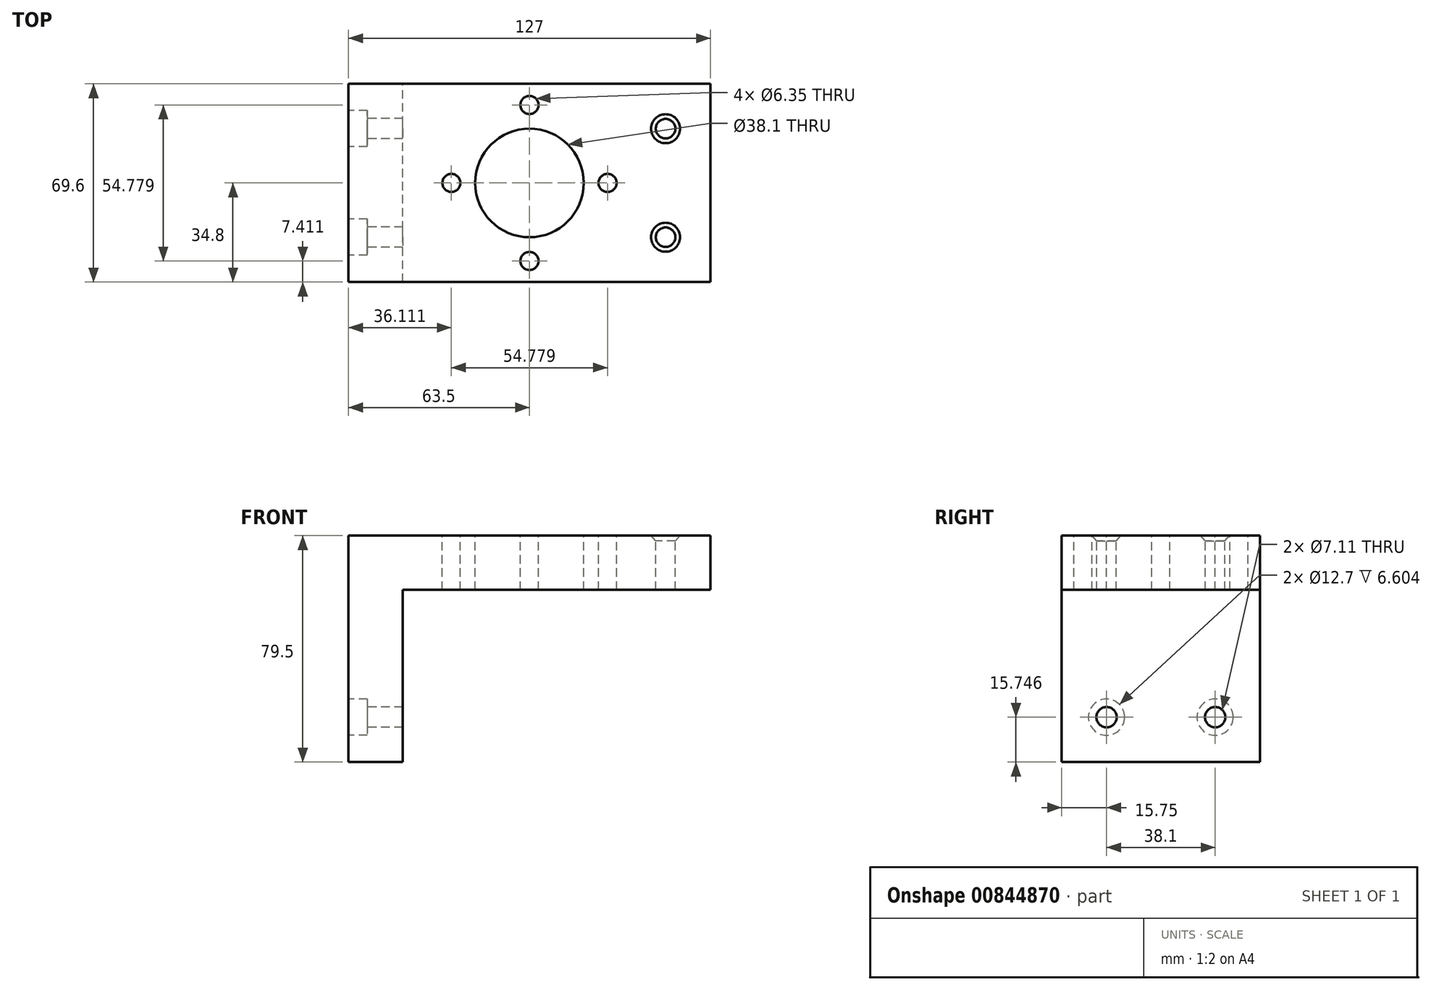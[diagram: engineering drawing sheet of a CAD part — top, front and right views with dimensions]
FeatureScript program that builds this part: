
annotation { "Feature Type Name" : "Feature", "Feature Type Description" : "" }
export const myFeature = defineFeature(function(context is Context, id is Id, definition is map)
    precondition{}
    {
        {
            var Q0;
            Q0=qCreatedBy(makeId("Top.planeOp"),FACE);
            var sketch = newSketch(context, id + "F0", { "sketchPlane" : qUnion([Q0])});
            skLineSegment(sketch, "E0.bottom", {"start": v(63.5, 34.8) * mm, "end": v(-63.5, 34.8) * mm});
            skLineSegment(sketch, "E0.top", {"start": v(63.5, -34.8) * mm, "end": v(-63.5, -34.8) * mm});
            skLineSegment(sketch, "E0.left", {"start": v(63.5, 34.8) * mm, "end": v(63.5, -34.8) * mm});
            skLineSegment(sketch, "E0.right", {"start": v(-63.5, 34.8) * mm, "end": v(-63.5, -34.8) * mm});
            skPoint(sketch, "E0.middle", {"position": v(0, 0) * mm});
            skSolve(sketch);
        }
        {
            var Q0;
            Q0 = qSketchRegion(id + "F0", true);
            extrude(context, id + "F1", {"entities" : qUnion([Q0]), "oppositeDirection" : true, "depth" : 19.05 * mm, "offsetDistance" : 25.4 * mm});
        }
        {
            var Q0;
            Q0=makeQuery(id+"F1.opExtrude","CAP_FACE",FACE,{"disambiguationData":[OSD([sQuery(id+"F0.wireOp",EDGE,"E0.bottom"),sQuery(id+"F0.wireOp",EDGE,"E0.top"),sQuery(id+"F0.wireOp",EDGE,"E0.left"),sQuery(id+"F0.wireOp",EDGE,"E0.right")])],"isStart":false});
            var sketch = newSketch(context, id + "F2", { "sketchPlane" : qUnion([Q0])});
            skLineSegment(sketch, "E1.bottom", {"start": v(-63.5, 34.8) * mm, "end": v(-44.45, 34.8) * mm});
            skLineSegment(sketch, "E1.top", {"start": v(-63.5, -34.8) * mm, "end": v(-44.45, -34.8) * mm});
            skLineSegment(sketch, "E1.left", {"start": v(-63.5, 34.8) * mm, "end": v(-63.5, -34.8) * mm});
            skLineSegment(sketch, "E1.right", {"start": v(-44.45, 34.8) * mm, "end": v(-44.45, -34.8) * mm});
            skSolve(sketch);
        }
        {
            var Q0;
            Q0 = qSketchRegion(id + "F2", true);
            extrude(context, id + "F3", {"entities" : qUnion([Q0]), "operationType" : NewBodyOperationType.ADD, "depth" : 60.45 * mm, "offsetDistance" : 25.4 * mm});
        }
        {
            var Q0;
            Q0=makeQuery(id+"F1.opExtrude","CAP_FACE",FACE,{"disambiguationData":[OSD([sQuery(id+"F0.wireOp",EDGE,"E0.bottom"),sQuery(id+"F0.wireOp",EDGE,"E0.top"),sQuery(id+"F0.wireOp",EDGE,"E0.left"),sQuery(id+"F0.wireOp",EDGE,"E0.right")])],"isStart":true});
            var sketch = newSketch(context, id + "F4", { "sketchPlane" : qUnion([Q0])});
            skCircle(sketch, "E2", {"center": v(0, 0) * mm, "radius": 19.05 * mm});
            skSolve(sketch);
        }
        {
            var Q0;
            Q0 = qSketchRegion(id + "F4", true);
            extrude(context, id + "F5", {"entities" : qUnion([Q0]), "operationType" : NewBodyOperationType.REMOVE, "oppositeDirection" : true, "depth" : 25.4 * mm, "offsetDistance" : 25.4 * mm});
        }
        {
            var Q0;
            Q0=makeQuery(id+"F1.opExtrude","CAP_FACE",FACE,{"disambiguationData":[OSD([sQuery(id+"F0.wireOp",EDGE,"E0.bottom"),sQuery(id+"F0.wireOp",EDGE,"E0.top"),sQuery(id+"F0.wireOp",EDGE,"E0.left"),sQuery(id+"F0.wireOp",EDGE,"E0.right")])],"isStart":true});
            var sketch = newSketch(context, id + "F6", { "sketchPlane" : qUnion([Q0])});
            skCircle(sketch, "E3", {"center": v(0, 0) * mm, "radius": 27.39 * mm});
            skCircle(sketch, "E4", {"center": v(0, 27.39) * mm, "radius": 3.18 * mm});
            skCircle(sketch, "E5.1.0", {"center": v(-27.39, 0) * mm, "radius": 3.18 * mm});
            skCircle(sketch, "E5.2.0", {"center": v(0, -27.39) * mm, "radius": 3.18 * mm});
            skCircle(sketch, "E5.3.0", {"center": v(27.39, 0) * mm, "radius": 3.18 * mm});
            skSolve(sketch);
        }
        {
            var Q0;
            {var subQ0=sQuery(id+"F6.wireOp",EDGE,"E4");var subQ1=sQuery(id+"F6.wireOp",EDGE,"E3");var subQ2=makeQuery(id+"F6.imprint","INTERSECT",VERTEX,{"disambiguationData":[OD(0.0)],"derivedFrom":[subQ1,subQ0]});Q0=makeQuery(id+"F6.imprint","IMPRINT",FACE,{"disambiguationData":[TD([[makeQuery(id+"F6.imprint","IMPRINT",EDGE,{"disambiguationData":[TD([[subQ2,-1.0]])],"derivedFrom":subQ1}),1.0]])]});}
            var Q1;
            {var subQ0=sQuery(id+"F6.wireOp",EDGE,"E4");var subQ1=sQuery(id+"F6.wireOp",EDGE,"E3");var subQ2=makeQuery(id+"F6.imprint","INTERSECT",VERTEX,{"disambiguationData":[OD(0.0)],"derivedFrom":[subQ1,subQ0]});Q1=makeQuery(id+"F6.imprint","IMPRINT",FACE,{"disambiguationData":[TD([[makeQuery(id+"F6.imprint","IMPRINT",EDGE,{"disambiguationData":[TD([[subQ2,-1.0]])],"derivedFrom":subQ1}),-1.0]])]});}
            var Q2;
            {var subQ0=sQuery(id+"F6.wireOp",EDGE,"E5.3.0");var subQ1=sQuery(id+"F6.wireOp",EDGE,"E3");var subQ2=makeQuery(id+"F6.imprint","INTERSECT",VERTEX,{"disambiguationData":[OD(0.0)],"derivedFrom":[subQ1,subQ0]});Q2=makeQuery(id+"F6.imprint","IMPRINT",FACE,{"disambiguationData":[TD([[makeQuery(id+"F6.imprint","IMPRINT",EDGE,{"disambiguationData":[TD([[subQ2,1.0]])],"derivedFrom":subQ1}),-1.0]])]});}
            var Q3;
            {var subQ0=sQuery(id+"F6.wireOp",EDGE,"E5.3.0");var subQ1=sQuery(id+"F6.wireOp",EDGE,"E3");var subQ2=makeQuery(id+"F6.imprint","INTERSECT",VERTEX,{"disambiguationData":[OD(0.0)],"derivedFrom":[subQ1,subQ0]});Q3=makeQuery(id+"F6.imprint","IMPRINT",FACE,{"disambiguationData":[TD([[makeQuery(id+"F6.imprint","IMPRINT",EDGE,{"disambiguationData":[TD([[subQ2,1.0]])],"derivedFrom":subQ1}),1.0]])]});}
            var Q4;
            {var subQ0=sQuery(id+"F6.wireOp",EDGE,"E5.2.0");var subQ1=sQuery(id+"F6.wireOp",EDGE,"E3");var subQ2=makeQuery(id+"F6.imprint","INTERSECT",VERTEX,{"disambiguationData":[OD(0.0)],"derivedFrom":[subQ1,subQ0]});Q4=makeQuery(id+"F6.imprint","IMPRINT",FACE,{"disambiguationData":[TD([[makeQuery(id+"F6.imprint","IMPRINT",EDGE,{"disambiguationData":[TD([[subQ2,-1.0]])],"derivedFrom":subQ1}),-1.0]])]});}
            var Q5;
            {var subQ0=sQuery(id+"F6.wireOp",EDGE,"E5.2.0");var subQ1=sQuery(id+"F6.wireOp",EDGE,"E3");var subQ2=makeQuery(id+"F6.imprint","INTERSECT",VERTEX,{"disambiguationData":[OD(0.0)],"derivedFrom":[subQ1,subQ0]});Q5=makeQuery(id+"F6.imprint","IMPRINT",FACE,{"disambiguationData":[TD([[makeQuery(id+"F6.imprint","IMPRINT",EDGE,{"disambiguationData":[TD([[subQ2,-1.0]])],"derivedFrom":subQ1}),1.0]])]});}
            var Q6;
            {var subQ0=sQuery(id+"F6.wireOp",EDGE,"E5.1.0");var subQ1=sQuery(id+"F6.wireOp",EDGE,"E3");var subQ2=makeQuery(id+"F6.imprint","INTERSECT",VERTEX,{"disambiguationData":[OD(0.0)],"derivedFrom":[subQ1,subQ0]});Q6=makeQuery(id+"F6.imprint","IMPRINT",FACE,{"disambiguationData":[TD([[makeQuery(id+"F6.imprint","IMPRINT",EDGE,{"disambiguationData":[TD([[subQ2,-1.0]])],"derivedFrom":subQ1}),1.0]])]});}
            var Q7;
            {var subQ0=sQuery(id+"F6.wireOp",EDGE,"E5.1.0");var subQ1=sQuery(id+"F6.wireOp",EDGE,"E3");var subQ2=makeQuery(id+"F6.imprint","INTERSECT",VERTEX,{"disambiguationData":[OD(0.0)],"derivedFrom":[subQ1,subQ0]});Q7=makeQuery(id+"F6.imprint","IMPRINT",FACE,{"disambiguationData":[TD([[makeQuery(id+"F6.imprint","IMPRINT",EDGE,{"disambiguationData":[TD([[subQ2,-1.0]])],"derivedFrom":subQ1}),-1.0]])]});}
            extrude(context, id + "F7", {"entities" : qUnion([Q0, Q1, Q2, Q3, Q4, Q5, Q6, Q7]), "operationType" : NewBodyOperationType.REMOVE, "oppositeDirection" : true, "depth" : 25.4 * mm, "offsetDistance" : 25.4 * mm});
        }
        {
            var Q0;
            Q0=makeQuery(id+"F1.opExtrude","CAP_FACE",FACE,{"disambiguationData":[OSD([sQuery(id+"F0.wireOp",EDGE,"E0.bottom"),sQuery(id+"F0.wireOp",EDGE,"E0.top"),sQuery(id+"F0.wireOp",EDGE,"E0.left"),sQuery(id+"F0.wireOp",EDGE,"E0.right")])],"isStart":true});
            var sketch = newSketch(context, id + "F8", { "sketchPlane" : qUnion([Q0])});
            skPoint(sketch, "E6", {"position": v(47.75, 19.05) * mm});
            skPoint(sketch, "E7", {"position": v(47.75, -19.05) * mm});
            skSolve(sketch);
        }
        {
            var Q0;
            Q0=sQuery(id+"F8.wireOp",VERTEX,"E6");
            var Q1;
            Q1=sQuery(id+"F8.wireOp",VERTEX,"E7");
            var Q2;
            Q2=makeQuery(id+"F1.opExtrude","SWEPT_BODY",BODY,{"disambiguationData":[OSD([sQuery(id+"F0.wireOp",EDGE,"E0.bottom"),sQuery(id+"F0.wireOp",EDGE,"E0.top"),sQuery(id+"F0.wireOp",EDGE,"E0.left"),sQuery(id+"F0.wireOp",EDGE,"E0.right")])]});
            hole(context, id + "F9", {"style" : HoleStyle.C_SINK, "endStyle" : HoleEndStyle.BLIND, "holeDiameter" : 6.86 * mm, "cSinkDiameter" : 10.16 * mm, "cSinkAngle" : 82 * degree, "majorDiameter" : 6.35 * mm, "holeDepth" : 25.4 * mm, "isTappedThrough" : true, "tappedDepth" : 12.7 * mm, "tapClearance" : 3, "startFromSketch" : true, "locations" : qUnion([Q0, Q1]), "scope" : qUnion([Q2])});
        }
        {
            var Q0;
            Q0=makeQuery(id+"F3.boolean.opBoolean","MERGE",FACE,{"derivedFrom":[makeQuery(id+"F1.opExtrude","SWEPT_FACE",FACE,{"disambiguationData":[OSD([sQuery(id+"F0.wireOp",EDGE,"E0.right")])]}),makeQuery(id+"F3.opExtrude","SWEPT_FACE",FACE,{"disambiguationData":[OSD([sQuery(id+"F2.wireOp",EDGE,"E1.left")])]})]});
            var sketch = newSketch(context, id + "F10", { "sketchPlane" : qUnion([Q0])});
            skPoint(sketch, "E8", {"position": v(-19.05, -63.75) * mm});
            skPoint(sketch, "E9", {"position": v(19.05, -63.75) * mm});
            skSolve(sketch);
        }
        {
            var Q0;
            Q0=sQuery(id+"F10.wireOp",VERTEX,"E8");
            var Q1;
            Q1=sQuery(id+"F10.wireOp",VERTEX,"E9");
            var Q2;
            Q2=makeQuery(id+"F1.opExtrude","SWEPT_BODY",BODY,{"disambiguationData":[OSD([sQuery(id+"F0.wireOp",EDGE,"E0.bottom"),sQuery(id+"F0.wireOp",EDGE,"E0.top"),sQuery(id+"F0.wireOp",EDGE,"E0.left"),sQuery(id+"F0.wireOp",EDGE,"E0.right")])]});
            hole(context, id + "F11", {"style" : HoleStyle.C_BORE, "endStyle" : HoleEndStyle.BLIND, "holeDiameter" : 7.11 * mm, "cBoreDiameter" : 12.7 * mm, "cBoreDepth" : 6.6 * mm, "majorDiameter" : 6.35 * mm, "holeDepth" : 25.4 * mm, "isTappedThrough" : true, "tappedDepth" : 12.7 * mm, "tapClearance" : 3, "startFromSketch" : true, "locations" : qUnion([Q0, Q1]), "scope" : qUnion([Q2])});
        }
    });
